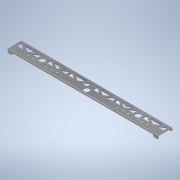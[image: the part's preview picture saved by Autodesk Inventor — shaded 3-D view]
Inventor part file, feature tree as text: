
AUTODESK INVENTOR PART (.ipt)
format: ipt  version: 2020 (Build 240168000, 168)  size: 466,432 bytes
history: native  units: in
note: dims shown in document units (in); Inventor stores cm internally (conversion verified against a paired STEP export)
features: extrude x1, fillet x1, sketch x1, other x1
ambient origin geometry x8: Origin, YZ Plane, XZ Plane, XY Plane, X Axis, Y Axis, Z Axis, Center Point
bodies: Solid1 (feature_tree)
feature tree (4):
  extrude  "Extrusion1"  Depth=0.375in
  fillet  "Fillet1"  Radius=0.375in
  sketch  "Sketch1"  dims[d0=0.375in d1=0.375in d2=0.375in d4=0.375in d5=0.375in d6=0.375in d7=0.375in d8=0.375in d9=0.375in d10=0.7874in d12=4.5in d13=0.3937in d15=1.0in d17=0.375in d18=0.32in d20=0.0in d21=0.0in d22=0.125in]
  other  "Cut-Extrude10"
